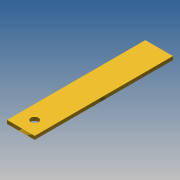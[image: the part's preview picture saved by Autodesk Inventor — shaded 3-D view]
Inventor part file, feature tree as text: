
AUTODESK INVENTOR PART (.ipt)
format: ipt  version: 2014 SP1 (Build 180222100, 222)  size: 84,480 bytes
history: native  units: in
note: dims shown in document units (in); Inventor stores cm internally (conversion verified against a paired STEP export)
features: extrude x2, sketch x2
ambient origin geometry x8: Origin, YZ Plane, XZ Plane, XY Plane, X Axis, Y Axis, Z Axis, Center Point
bodies: Solid1 (feature_tree)
feature tree (4):
  extrude  "Extrusion1"  Depth=10.0in
  extrude  "Extrusion2"  Depth=0.25in
  sketch  "Sketch1"  dims[d0=2.0in d1=10.0in]
  sketch  "Sketch2"  dims[d2=0.25in d3=0.0in d4=1.0in d5=1.0in d6=0.0in]
